FCSTD DOCUMENT  (FreeCAD 0.19R19443 (Git))
Label: M-19_v100k_ohp
License: Creative Commons Attribution
LicenseURL: http://creativecommons.org/licenses/by/4.0/
objects: Sketcher::SketchObject×1
note: 1 computed .brp shape members not serialized (recipe doc carries the construction recipe); baked Part::Feature solids carry a one-line shape summary decoded from their .brp

FEATURE [Sketcher::SketchObject] Sketch
  sketch-geometry (14):
    g0: LineSegment StartX=-138.5 StartY=105 StartZ=0 EndX=138.5 EndY=105 EndZ=0
    g1: LineSegment StartX=148.5 StartY=95 StartZ=0 EndX=148.5 EndY=-65 EndZ=0
    g2: LineSegment StartX=108.5 StartY=-105 StartZ=0 EndX=-108.5 EndY=-105 EndZ=0
    g3: LineSegment StartX=-148.5 StartY=-65 StartZ=0 EndX=-148.5 EndY=95 EndZ=0
    g4: ArcOfCircle CenterX=-108.5 CenterY=-65 CenterZ=0 NormalX=0 NormalY=0 NormalZ=1 AngleXU=0 Radius=40 StartAngle=3.14159 EndAngle=4.71239
    g5: ArcOfCircle CenterX=108.5 CenterY=-65 CenterZ=0 NormalX=0 NormalY=0 NormalZ=1 AngleXU=0 Radius=40 StartAngle=4.71239 EndAngle=6.28319
    g6: ArcOfCircle CenterX=-138.5 CenterY=95 CenterZ=0 NormalX=0 NormalY=0 NormalZ=1 AngleXU=0 Radius=10 StartAngle=1.5708 EndAngle=3.14159
    g7: ArcOfCircle CenterX=138.5 CenterY=95 CenterZ=0 NormalX=0 NormalY=0 NormalZ=1 AngleXU=0 Radius=10 StartAngle=-9e-16 EndAngle=1.5708
    g8: Circle CenterX=-120 CenterY=92 CenterZ=0 NormalX=0 NormalY=0 NormalZ=1 AngleXU=0 Radius=3
    g9: Circle CenterX=-80 CenterY=93 CenterZ=0 NormalX=0 NormalY=0 NormalZ=1 AngleXU=0 Radius=3
    g10: Circle CenterX=-40 CenterY=93 CenterZ=0 NormalX=0 NormalY=0 NormalZ=1 AngleXU=0 Radius=3
    g11: Circle CenterX=40 CenterY=93 CenterZ=0 NormalX=0 NormalY=0 NormalZ=1 AngleXU=0 Radius=3
    g12: Circle CenterX=80 CenterY=93 CenterZ=0 NormalX=0 NormalY=0 NormalZ=1 AngleXU=0 Radius=3
    g13: Circle CenterX=120 CenterY=92 CenterZ=0 NormalX=0 NormalY=0 NormalZ=1 AngleXU=0 Radius=3
  constraints (36):
    c: Horizontal(g2)
    c: Vertical(g3)
    c: Tangent(g2,g4) = 1.5708
    c: Tangent(g3,g4) = 1.5708
    c: Tangent(g2,g5) = 1.5708
    c: Tangent(g1,g5) = 1.5708
    c: Equal(g5,g4)
    c: Radius(g4) = 40
    c: Tangent(g0,g6) = 1.5708
    c: Tangent(g3,g6) = 1.5708
    c: Tangent(g1,g7) = 1.5708
    c: Tangent(g0,g7) = 1.5708
    c: Equal(g7,g6)
    c: Radius(g6) = 10
    c: DistanceX(g3,g1) = 297
    c: DistanceY(g2,g0) = 210
    c: Horizontal(g0)
    c: Symmetric(g3,g1,g-2)
    c: DistanceY(g-1,g0) = 105
    c: Radius(g13) = 3
    c: Equal(g13,g12)
    c: Equal(g13,g11)
    c: Equal(g13,g10)
    c: Equal(g13,g9)
    c: Equal(g13,g8)
    c: DistanceY(g8,g9) = 1
    c: DistanceY(g9,g10) = 0
    c: DistanceY(g11,g12) = 0
    c: DistanceY(g13,g12) = 1
    c: DistanceX(g12,g13) = 40
    c: DistanceX(g11,g12) = 40
    c: DistanceX(g10,g11) = 80
    c: DistanceX(g9,g10) = 40
    c: DistanceX(g8,g9) = 40
    c: Symmetric(g10,g11,g-2)
    c: Distance(g11,g0) = 12
